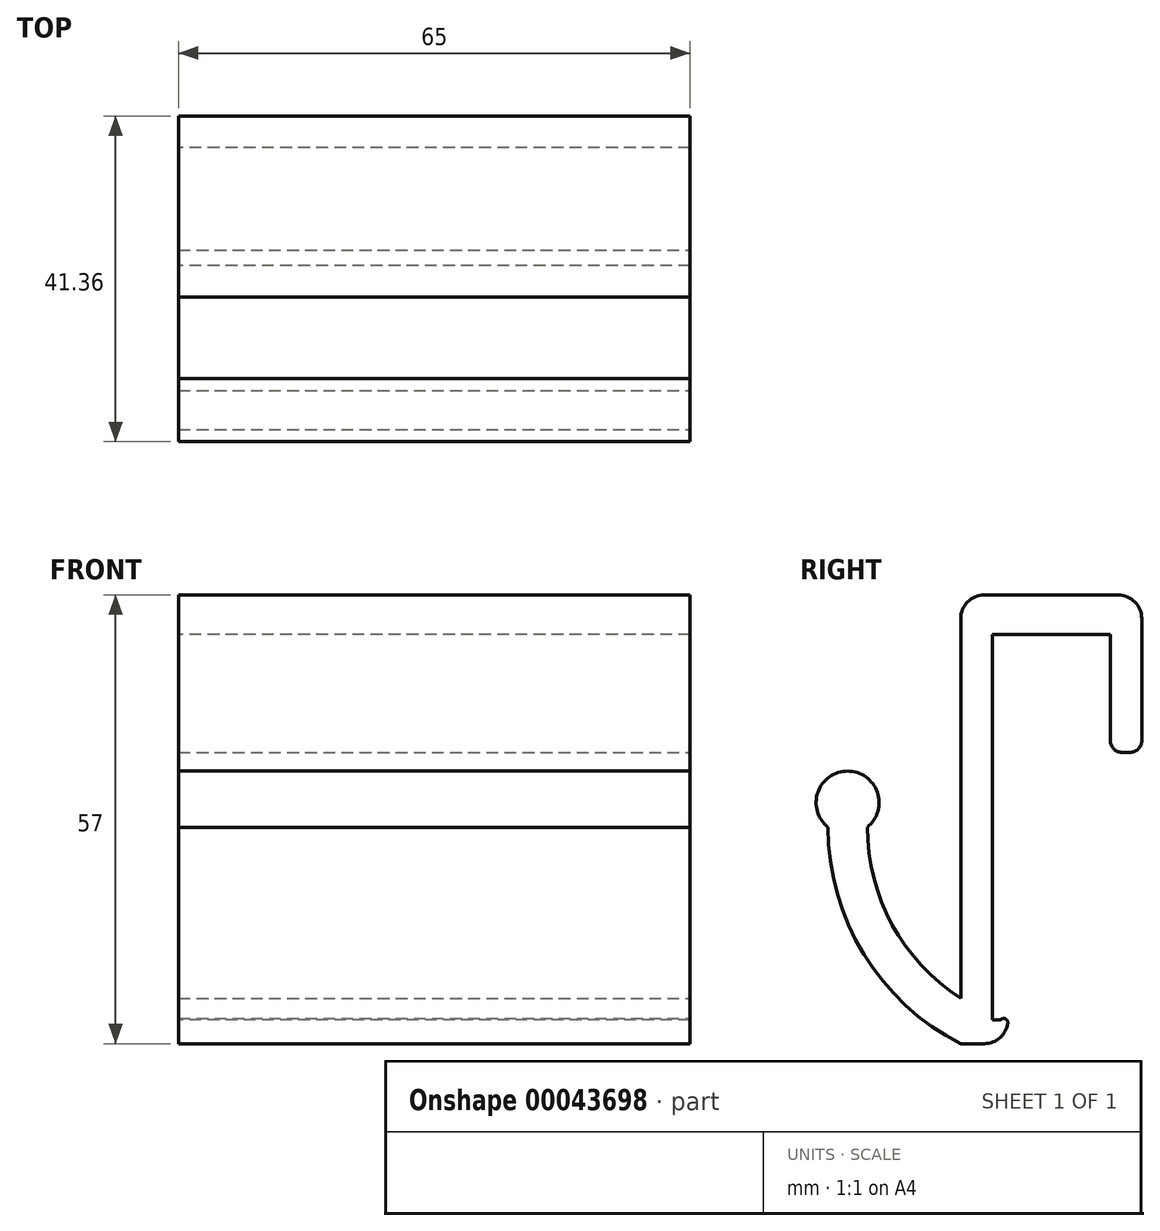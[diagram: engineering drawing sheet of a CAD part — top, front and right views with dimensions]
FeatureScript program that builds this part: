
annotation { "Feature Type Name" : "Feature", "Feature Type Description" : "" }
export const myFeature = defineFeature(function(context is Context, id is Id, definition is map)
    precondition{}
    {
        {
            var Q0;
            Q0=qCreatedBy(makeId("Front.planeOp"),FACE);
            var sketch = newSketch(context, id + "F0", { "sketchPlane" : qUnion([Q0])});
            skLineSegment(sketch, "E0.rect.bottom", {"start": v(32.5, -24.5) * mm, "end": v(-32.5, -24.5) * mm});
            skLineSegment(sketch, "E0.rect.top", {"start": v(32.5, 24.5) * mm, "end": v(-32.5, 24.5) * mm});
            skLineSegment(sketch, "E0.rect.left", {"start": v(32.5, -24.5) * mm, "end": v(32.5, 24.5) * mm});
            skLineSegment(sketch, "E0.rect.right", {"start": v(-32.5, -24.5) * mm, "end": v(-32.5, 24.5) * mm});
            skPoint(sketch, "E0.rect.middle", {"position": v(0, 0) * mm});
            skLineSegment(sketch, "E1", {"start": v(-32.5, 24.5) * mm, "end": v(-32.5, 29.5) * mm});
            skLineSegment(sketch, "E2", {"start": v(-32.5, 29.5) * mm, "end": v(32.5, 29.5) * mm});
            skLineSegment(sketch, "E3", {"start": v(32.5, 29.5) * mm, "end": v(32.5, 24.5) * mm});
            skLineSegment(sketch, "E4", {"start": v(32.5, -24.5) * mm, "end": v(32.5, -27.5) * mm});
            skLineSegment(sketch, "E5", {"start": v(32.5, -27.5) * mm, "end": v(-32.5, -27.5) * mm});
            skLineSegment(sketch, "E6", {"start": v(-32.5, -27.5) * mm, "end": v(-32.5, -24.5) * mm});
            skSolve(sketch);
        }
        {
            var Q0;
            Q0=makeQuery(id+"F0.imprint","IMPRINT",FACE,{"disambiguationData":[TD([[makeQuery(id+"F0.imprint","IMPRINT",EDGE,{"derivedFrom":sQuery(id+"F0.wireOp",EDGE,"E0.rect.bottom")}),-1.0]])]});
            var Q1;
            Q1=makeQuery(id+"F0.imprint","IMPRINT",FACE,{"disambiguationData":[TD([[makeQuery(id+"F0.imprint","IMPRINT",EDGE,{"derivedFrom":sQuery(id+"F0.wireOp",EDGE,"E0.rect.top")}),-1.0]])]});
            var Q2;
            Q2=makeQuery(id+"F0.imprint","IMPRINT",FACE,{"disambiguationData":[TD([[makeQuery(id+"F0.imprint","IMPRINT",EDGE,{"derivedFrom":sQuery(id+"F0.wireOp",EDGE,"E0.rect.bottom")}),1.0]])]});
            extrude(context, id + "F1", {"entities" : qUnion([Q0, Q1, Q2]), "depth" : 4 * mm});
        }
        {
            var Q0;
            Q0=makeQuery(id+"F0.imprint","IMPRINT",FACE,{"disambiguationData":[TD([[makeQuery(id+"F0.imprint","IMPRINT",EDGE,{"derivedFrom":sQuery(id+"F0.wireOp",EDGE,"E0.rect.top")}),-1.0]])]});
            extrude(context, id + "F2", {"entities" : qUnion([Q0]), "operationType" : NewBodyOperationType.ADD, "oppositeDirection" : true, "depth" : 15 * mm});
        }
        {
            var Q0;
            Q0=makeQuery(id+"F0.imprint","IMPRINT",FACE,{"disambiguationData":[TD([[makeQuery(id+"F0.imprint","IMPRINT",EDGE,{"derivedFrom":sQuery(id+"F0.wireOp",EDGE,"E0.rect.bottom")}),1.0]])]});
            extrude(context, id + "F3", {"entities" : qUnion([Q0]), "operationType" : NewBodyOperationType.ADD, "oppositeDirection" : true, "depth" : 1 * mm});
        }
        {
            var Q0;
            {var subQ0=sQuery(id+"F0.wireOp",EDGE,"E3");var subQ1=sQuery(id+"F0.wireOp",EDGE,"E4");Q0=makeQuery(id+"F3.boolean.opBoolean","MERGE",FACE,{"derivedFrom":[makeQuery(id+"F2.boolean.opBoolean","MERGE",FACE,{"derivedFrom":[makeQuery(id+"F1.opExtrude","SWEPT_FACE",FACE,{"disambiguationData":[OSD([sQuery(id+"F0.wireOp",EDGE,"E0.rect.left"),subQ0,subQ1])]}),makeQuery(id+"F2.opExtrude","SWEPT_FACE",FACE,{"disambiguationData":[OSD([subQ0])]})]}),makeQuery(id+"F3.opExtrude","SWEPT_FACE",FACE,{"disambiguationData":[OSD([subQ1])]})]});}
            var sketch = newSketch(context, id + "F4", { "sketchPlane" : qUnion([Q0])});
            skLineSegment(sketch, "E7", {"start": v(15, 29.5) * mm, "end": v(15, 9.5) * mm});
            skLineSegment(sketch, "E8", {"start": v(15, 9.5) * mm, "end": v(19, 9.5) * mm});
            skLineSegment(sketch, "E9", {"start": v(19, 9.5) * mm, "end": v(19, 29.5) * mm});
            skLineSegment(sketch, "E10", {"start": v(19, 29.5) * mm, "end": v(15, 29.5) * mm});
            skLineSegment(sketch, "E11", {"start": v(1, -27.5) * mm, "end": v(2, -27.5) * mm});
            skLineSegment(sketch, "E12", {"start": v(2, -27.5) * mm, "end": v(2, -23.92) * mm});
            skLineSegment(sketch, "E13", {"start": v(2, -23.92) * mm, "end": v(1, -24.5) * mm});
            skLineSegment(sketch, "E14", {"start": v(1, -24.5) * mm, "end": v(1, -27.5) * mm});
            skArc(sketch, "E15", {"start": v(-20.86, 0) * mm, "mid": v(-16.3, -16.13) * mm, "end": v(-4, -27.5) * mm});
            skArc(sketch, "E16", {"start": v(-15.86, 0) * mm, "mid": v(-12.7, -12.38) * mm, "end": v(-4, -21.74) * mm});
            skLineSegment(sketch, "E17", {"start": v(-20.86, 0) * mm, "end": v(10, 0) * mm, "construction": true});
            skArc(sketch, "E18", {"start": v(-15.86, 0) * mm, "mid": v(-18.36, 7.12) * mm, "end": v(-20.86, 0) * mm});
            skSolve(sketch);
        }
        {
            var Q0;
            Q0 = qSketchRegion(id + "F4", true);
            var Q1;
            {var subQ4=sQuery(id+"F4.wireOp",EDGE,"E15");Q1=makeQuery(id+"F4.imprint","IMPRINT",FACE,{"disambiguationData":[TD([[makeQuery(id+"F4.imprint","IMPRINT",EDGE,{"derivedFrom":subQ4}),1.0]])]});}
            var Q2;
            {var subQ0=sQuery(id+"F0.wireOp",EDGE,"E1");var subQ1=sQuery(id+"F0.wireOp",EDGE,"E6");Q2=makeQuery(id+"F3.boolean.opBoolean","MERGE",FACE,{"derivedFrom":[makeQuery(id+"F2.boolean.opBoolean","MERGE",FACE,{"derivedFrom":[makeQuery(id+"F1.opExtrude","SWEPT_FACE",FACE,{"disambiguationData":[OSD([sQuery(id+"F0.wireOp",EDGE,"E0.rect.right"),subQ0,subQ1])]}),makeQuery(id+"F2.opExtrude","SWEPT_FACE",FACE,{"disambiguationData":[OSD([subQ0])]})]}),makeQuery(id+"F3.opExtrude","SWEPT_FACE",FACE,{"disambiguationData":[OSD([subQ1])]})]});}
            extrude(context, id + "F5", {"entities" : qUnion([Q0, Q1]), "operationType" : NewBodyOperationType.ADD, "endBound" : BoundingType.UP_TO_SURFACE, "oppositeDirection" : true, "endBoundEntityFace" : qUnion([Q2]), "depth" : 25 * mm});
        }
        {
            var Q0;
            Q0=makeQuery(id+"F5.opExtrude","SWEPT_EDGE",EDGE,{"disambiguationData":[OSD([sQuery(id+"F4.wireOp",EDGE,"E9"),sQuery(id+"F4.wireOp",EDGE,"E10")])]});
            var Q1;
            Q1=makeQuery(id+"F1.opExtrude","CAP_EDGE",EDGE,{"disambiguationData":[OSD([sQuery(id+"F0.wireOp",EDGE,"E2")])],"isStart":false});
            var Q2;
            Q2=makeQuery(id+"F5.opExtrude","SWEPT_EDGE",EDGE,{"disambiguationData":[OSD([sQuery(id+"F4.wireOp",EDGE,"E11"),sQuery(id+"F4.wireOp",EDGE,"E12")])]});
            var Q3;
            Q3=makeQuery(id+"F5.opExtrude","SWEPT_EDGE",EDGE,{"disambiguationData":[OSD([sQuery(id+"F0.wireOp",EDGE,"E0.rect.left"),sQuery(id+"F0.wireOp",EDGE,"E3"),sQuery(id+"F0.wireOp",EDGE,"E4"),sQuery(id+"F4.wireOp",EDGE,"ea8893f4-6408-4d1f-b56b-d2168bf36e3d")])]});
            fillet(context, id + "F6", {"entities" : qUnion([Q0, Q1, Q2, Q3]), "radius" : 3 * mm, "tangentPropagation" : true, "allowEdgeOverflow" : false});
        }
        {
            var Q0;
            Q0=makeQuery(id+"F2.opExtrude","CAP_EDGE",EDGE,{"disambiguationData":[OSD([sQuery(id+"F0.wireOp",EDGE,"E0.rect.top")])],"isStart":false});
            var Q1;
            Q1=makeQuery(id+"F2.opExtrude","CAP_EDGE",EDGE,{"disambiguationData":[OSD([sQuery(id+"F0.wireOp",EDGE,"E0.rect.top")])],"isStart":true});
            var Q2;
            Q2=makeQuery(id+"F3.opExtrude","CAP_EDGE",EDGE,{"disambiguationData":[OSD([sQuery(id+"F0.wireOp",EDGE,"E0.rect.bottom")])],"isStart":true});
            var Q3;
            {var subQ0=sQuery(id+"F0.wireOp",EDGE,"E0.rect.bottom");Q3=makeQuery(id+"F5.boolean.opBoolean","MERGE",EDGE,{"derivedFrom":[makeQuery(id+"F3.opExtrude","CAP_EDGE",EDGE,{"disambiguationData":[OSD([subQ0])],"isStart":false}),makeQuery(id+"F5.opExtrude","SWEPT_EDGE",EDGE,{"disambiguationData":[OSD([subQ0,sQuery(id+"F0.wireOp",EDGE,"E0.rect.left"),sQuery(id+"F0.wireOp",EDGE,"E4"),sQuery(id+"F4.wireOp",EDGE,"E13"),sQuery(id+"F4.wireOp",EDGE,"E14")])]})]});}
            var Q4;
            Q4=makeQuery(id+"F5.opExtrude","SWEPT_EDGE",EDGE,{"disambiguationData":[OSD([sQuery(id+"F4.wireOp",EDGE,"E12"),sQuery(id+"F4.wireOp",EDGE,"E13")])]});
            fillet(context, id + "F7", {"entities" : qUnion([Q0, Q1, Q2, Q3, Q4]), "radius" : 0.5 * mm, "tangentPropagation" : true, "allowEdgeOverflow" : false});
        }
        {
            var Q0;
            Q0=makeQuery(id+"F5.opExtrude","SWEPT_EDGE",EDGE,{"disambiguationData":[OSD([sQuery(id+"F4.wireOp",EDGE,"E7"),sQuery(id+"F4.wireOp",EDGE,"E8")])]});
            var Q1;
            Q1=makeQuery(id+"F5.opExtrude","SWEPT_EDGE",EDGE,{"disambiguationData":[OSD([sQuery(id+"F4.wireOp",EDGE,"E8"),sQuery(id+"F4.wireOp",EDGE,"E9")])]});
            var Q2;
            Q2=makeQuery(id+"F5.opExtrude","SWEPT_EDGE",EDGE,{"disambiguationData":[OSD([sQuery(id+"F4.wireOp",EDGE,"ea8893f4-6408-4d1f-b56b-d2168bf36e3d"),sQuery(id+"F4.wireOp",EDGE,"fcd73a69-4350-4eb9-ac6e-9daeea31be28")])]});
            var Q3;
            Q3=makeQuery(id+"F5.opExtrude","SWEPT_EDGE",EDGE,{"disambiguationData":[OSD([sQuery(id+"F4.wireOp",EDGE,"13445d1f-a1cf-4193-8990-ddddebb34eff"),sQuery(id+"F4.wireOp",EDGE,"fcd73a69-4350-4eb9-ac6e-9daeea31be28")])]});
            fillet(context, id + "F8", {"entities" : qUnion([Q0, Q1, Q2, Q3]), "radius" : 1.5 * mm, "tangentPropagation" : true, "allowEdgeOverflow" : false});
        }
    });
